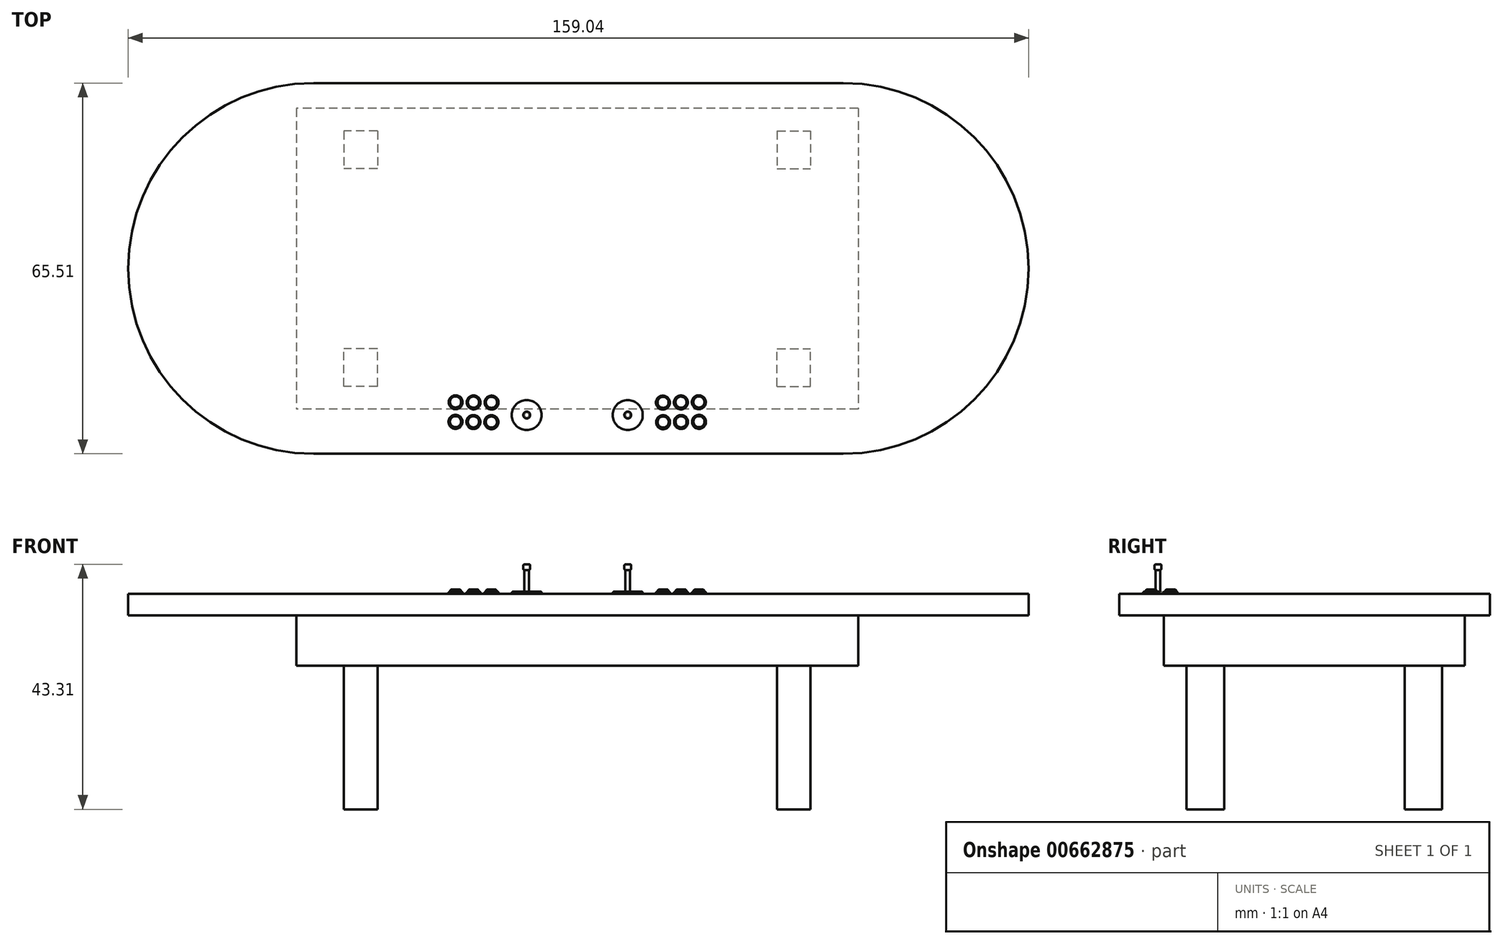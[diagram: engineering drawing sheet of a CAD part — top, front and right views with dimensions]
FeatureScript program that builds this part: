
annotation { "Feature Type Name" : "Feature", "Feature Type Description" : "" }
export const myFeature = defineFeature(function(context is Context, id is Id, definition is map)
    precondition{}
    {
        {
            var Q0;
            Q0=qCreatedBy(makeId("Top.planeOp"),FACE);
            var sketch = newSketch(context, id + "F0", { "sketchPlane" : qUnion([Q0])});
            skLineSegment(sketch, "E0.bottom", {"start": v(-46.56, 31.03) * mm, "end": v(46.96, 31.03) * mm});
            skLineSegment(sketch, "E0.top", {"start": v(-46.56, -34.48) * mm, "end": v(46.96, -34.48) * mm});
            skLineSegment(sketch, "E0.left", {"start": v(-46.56, 31.03) * mm, "end": v(-46.56, -34.48) * mm});
            skLineSegment(sketch, "E0.right", {"start": v(46.96, 31.03) * mm, "end": v(46.96, -34.48) * mm});
            skArc(sketch, "E1", {"start": v(46.96, 31.03) * mm, "mid": v(79.72, -1.72) * mm, "end": v(46.96, -34.48) * mm});
            skArc(sketch, "E2", {"start": v(-46.56, -34.48) * mm, "mid": v(-79.32, -1.72) * mm, "end": v(-46.56, 31.03) * mm});
            skSolve(sketch);
        }
        {
            var Q0;
            Q0=makeQuery(id+"F0.imprint","IMPRINT",FACE,{"disambiguationData":[TD([[makeQuery(id+"F0.imprint","IMPRINT",EDGE,{"derivedFrom":sQuery(id+"F0.wireOp",EDGE,"E0.bottom")}),-1.0]])]});
            var Q1;
            Q1=makeQuery(id+"F0.imprint","IMPRINT",FACE,{"disambiguationData":[TD([[makeQuery(id+"F0.imprint","IMPRINT",EDGE,{"derivedFrom":sQuery(id+"F0.wireOp",EDGE,"E0.left")}),-1.0]])]});
            var Q2;
            Q2=makeQuery(id+"F0.imprint","IMPRINT",FACE,{"disambiguationData":[TD([[makeQuery(id+"F0.imprint","IMPRINT",EDGE,{"derivedFrom":sQuery(id+"F0.wireOp",EDGE,"E0.right")}),1.0]])]});
            extrude(context, id + "F1", {"entities" : qUnion([Q0, Q1, Q2]), "depth" : 3.8 * mm, "offsetDistance" : 25.4 * mm});
        }
        {
            var Q0;
            Q0=makeQuery(id+"F1.opExtrude","CAP_FACE",FACE,{"disambiguationData":[OSD([sQuery(id+"F0.wireOp",EDGE,"E0.bottom"),sQuery(id+"F0.wireOp",EDGE,"E0.top"),sQuery(id+"F0.wireOp",EDGE,"E1"),sQuery(id+"F0.wireOp",EDGE,"E2")])],"isStart":true});
            var sketch = newSketch(context, id + "F2", { "sketchPlane" : qUnion([Q0])});
            skLineSegment(sketch, "E3.bottom", {"start": v(49.64, -26.58) * mm, "end": v(-49.64, -26.58) * mm});
            skLineSegment(sketch, "E3.top", {"start": v(49.64, 26.58) * mm, "end": v(-49.64, 26.58) * mm});
            skLineSegment(sketch, "E3.left", {"start": v(49.64, -26.58) * mm, "end": v(49.64, 26.58) * mm});
            skLineSegment(sketch, "E3.right", {"start": v(-49.64, -26.58) * mm, "end": v(-49.64, 26.58) * mm});
            skPoint(sketch, "E3.middle", {"position": v(0, 0) * mm});
            skSolve(sketch);
        }
        {
            var Q0;
            Q0 = qSketchRegion(id + "F2", true);
            extrude(context, id + "F3", {"entities" : qUnion([Q0]), "operationType" : NewBodyOperationType.ADD, "depth" : 8.9 * mm, "offsetDistance" : 25.4 * mm});
        }
        {
            var Q0;
            Q0=makeQuery(id+"F3.opExtrude","CAP_FACE",FACE,{"disambiguationData":[OSD([sQuery(id+"F2.wireOp",EDGE,"E3.bottom"),sQuery(id+"F2.wireOp",EDGE,"E3.top"),sQuery(id+"F2.wireOp",EDGE,"E3.left"),sQuery(id+"F2.wireOp",EDGE,"E3.right")])],"isStart":false});
            var sketch = newSketch(context, id + "F4", { "sketchPlane" : qUnion([Q0])});
            skLineSegment(sketch, "E4.bottom", {"start": v(-35.3, 22.55) * mm, "end": v(-41.22, 22.55) * mm});
            skLineSegment(sketch, "E4.top", {"start": v(-35.3, 15.93) * mm, "end": v(-41.22, 15.93) * mm});
            skLineSegment(sketch, "E4.left", {"start": v(-35.3, 22.55) * mm, "end": v(-35.3, 15.93) * mm});
            skLineSegment(sketch, "E4.right", {"start": v(-41.22, 22.55) * mm, "end": v(-41.22, 15.93) * mm});
            skPoint(sketch, "E4.middle", {"position": v(-38.26, 19.24) * mm});
            skLineSegment(sketch, "E5", {"start": v(0, 26.58) * mm, "end": v(0, -26.58) * mm, "construction": true});
            skLineSegment(sketch, "E6.MirrorCS", {"start": v(35.3, 22.55) * mm, "end": v(35.3, 15.93) * mm});
            skLineSegment(sketch, "E7.MirrorCS", {"start": v(35.3, 22.55) * mm, "end": v(41.22, 22.55) * mm});
            skLineSegment(sketch, "E8.MirrorCS", {"start": v(41.22, 22.55) * mm, "end": v(41.22, 15.93) * mm});
            skLineSegment(sketch, "E9.MirrorCS", {"start": v(35.3, 15.93) * mm, "end": v(41.22, 15.93) * mm});
            skLineSegment(sketch, "E10", {"start": v(-49.64, 0) * mm, "end": v(49.64, 0) * mm, "construction": true});
            skLineSegment(sketch, "E11.MirrorCS", {"start": v(-35.3, -15.93) * mm, "end": v(-41.22, -15.93) * mm});
            skLineSegment(sketch, "E12.MirrorCS", {"start": v(-41.22, -22.55) * mm, "end": v(-41.22, -15.93) * mm});
            skLineSegment(sketch, "E13.MirrorCS", {"start": v(-35.3, -22.55) * mm, "end": v(-41.22, -22.55) * mm});
            skLineSegment(sketch, "E14.MirrorCS", {"start": v(-35.3, -22.55) * mm, "end": v(-35.3, -15.93) * mm});
            skLineSegment(sketch, "E15.MirrorCS", {"start": v(35.3, -15.93) * mm, "end": v(41.22, -15.93) * mm});
            skLineSegment(sketch, "E16.MirrorCS", {"start": v(35.3, -22.55) * mm, "end": v(35.3, -15.93) * mm});
            skLineSegment(sketch, "E17.MirrorCS", {"start": v(35.3, -22.55) * mm, "end": v(41.22, -22.55) * mm});
            skLineSegment(sketch, "E18.MirrorCS", {"start": v(41.22, -22.55) * mm, "end": v(41.22, -15.93) * mm});
            skSolve(sketch);
        }
        {
            var Q0;
            Q0=makeQuery(id+"F4.imprint","IMPRINT",FACE,{"disambiguationData":[TD([[makeQuery(id+"F4.imprint","IMPRINT",EDGE,{"derivedFrom":sQuery(id+"F4.wireOp",EDGE,"E4.bottom")}),1.0]])]});
            var Q1;
            Q1=makeQuery(id+"F4.imprint","IMPRINT",FACE,{"disambiguationData":[TD([[makeQuery(id+"F4.imprint","IMPRINT",EDGE,{"derivedFrom":sQuery(id+"F4.wireOp",EDGE,"E6.MirrorCS")}),1.0]])]});
            var Q2;
            Q2=makeQuery(id+"F4.imprint","IMPRINT",FACE,{"disambiguationData":[TD([[makeQuery(id+"F4.imprint","IMPRINT",EDGE,{"derivedFrom":sQuery(id+"F4.wireOp",EDGE,"E15.MirrorCS")}),-1.0]])]});
            var Q3;
            Q3=makeQuery(id+"F4.imprint","IMPRINT",FACE,{"disambiguationData":[TD([[makeQuery(id+"F4.imprint","IMPRINT",EDGE,{"derivedFrom":sQuery(id+"F4.wireOp",EDGE,"E11.MirrorCS")}),1.0]])]});
            var Q4;
            Q4=sQuery(id+"F4.wireOp",EDGE,"E4.left");
            var Q5;
            Q5=sQuery(id+"F4.wireOp",EDGE,"E4.top");
            var Q6;
            Q6=sQuery(id+"F4.wireOp",EDGE,"E4.right");
            var Q7;
            Q7=sQuery(id+"F4.wireOp",EDGE,"E4.bottom");
            extrude(context, id + "F5", {"entities" : qUnion([Q0, Q1, Q2, Q3]), "operationType" : NewBodyOperationType.ADD, "surfaceEntities" : qUnion([Q4, Q5, Q6, Q7]), "depth" : 25.4 * mm, "offsetDistance" : 25.4 * mm});
        }
        {
            var Q0;
            Q0=makeQuery(id+"F1.opExtrude","CAP_FACE",FACE,{"disambiguationData":[OSD([sQuery(id+"F0.wireOp",EDGE,"E0.bottom"),sQuery(id+"F0.wireOp",EDGE,"E0.top"),sQuery(id+"F0.wireOp",EDGE,"E1"),sQuery(id+"F0.wireOp",EDGE,"E2")])],"isStart":false});
            var sketch = newSketch(context, id + "F6", { "sketchPlane" : qUnion([Q0])});
            skCircle(sketch, "E19", {"center": v(-15.16, -28.9) * mm, "radius": 1.23 * mm});
            skCircle(sketch, "E20.0.1.0", {"center": v(-15.13, -25.42) * mm, "radius": 1.23 * mm});
            skCircle(sketch, "E20.1.0.0", {"center": v(-18.34, -28.86) * mm, "radius": 1.23 * mm});
            skCircle(sketch, "E20.1.1.0", {"center": v(-18.3, -25.4) * mm, "radius": 1.23 * mm});
            skCircle(sketch, "E20.2.0.0", {"center": v(-21.5, -28.83) * mm, "radius": 1.23 * mm});
            skCircle(sketch, "E20.2.1.0", {"center": v(-21.48, -25.36) * mm, "radius": 1.23 * mm});
            skLineSegment(sketch, "E20.direction1", {"start": v(-15.16, -28.9) * mm, "end": v(-18.34, -28.86) * mm, "construction": true});
            skLineSegment(sketch, "E20.direction2", {"start": v(-15.16, -28.9) * mm, "end": v(-15.13, -25.42) * mm, "construction": true});
            skLineSegment(sketch, "E21", {"start": v(0, -30.78) * mm, "end": v(0, -16.96) * mm, "construction": true});
            skCircle(sketch, "E22.MirrorC", {"center": v(21.5, -28.83) * mm, "radius": 1.23 * mm});
            skCircle(sketch, "E23.MirrorC", {"center": v(18.34, -28.86) * mm, "radius": 1.23 * mm});
            skCircle(sketch, "E24.MirrorC", {"center": v(21.48, -25.36) * mm, "radius": 1.23 * mm});
            skCircle(sketch, "E25.MirrorC", {"center": v(18.3, -25.4) * mm, "radius": 1.23 * mm});
            skCircle(sketch, "E26.MirrorC", {"center": v(15.13, -25.42) * mm, "radius": 1.23 * mm});
            skCircle(sketch, "E27.MirrorC", {"center": v(15.16, -28.9) * mm, "radius": 1.23 * mm});
            skCircle(sketch, "E28", {"center": v(8.92, -27.62) * mm, "radius": 2.64 * mm});
            skCircle(sketch, "E29.MirrorC", {"center": v(-8.92, -27.62) * mm, "radius": 2.64 * mm});
            skSolve(sketch);
        }
        {
            var Q0;
            Q0 = qSketchRegion(id + "F6", true);
            extrude(context, id + "F7", {"entities" : qUnion([Q0]), "operationType" : NewBodyOperationType.ADD, "depth" : 0.38 * mm, "offsetDistance" : 25.4 * mm});
        }
        {
            var Q0;
            Q0=makeQuery(id+"F7.opExtrude","CAP_FACE",FACE,{"disambiguationData":[OSD([sQuery(id+"F6.wireOp",EDGE,"E28")])],"isStart":false});
            var sketch = newSketch(context, id + "F8", { "sketchPlane" : qUnion([Q0])});
            skCircle(sketch, "E30", {"center": v(21.5, -28.8) * mm, "radius": 0.98 * mm});
            skCircle(sketch, "E31.0.1.0", {"center": v(21.5, -25.32) * mm, "radius": 0.98 * mm});
            skCircle(sketch, "E31.1.0.0", {"center": v(18.34, -28.83) * mm, "radius": 0.98 * mm});
            skCircle(sketch, "E31.1.1.0", {"center": v(18.33, -25.35) * mm, "radius": 0.98 * mm});
            skCircle(sketch, "E31.2.0.0", {"center": v(15.17, -28.86) * mm, "radius": 0.98 * mm});
            skCircle(sketch, "E31.2.1.0", {"center": v(15.16, -25.38) * mm, "radius": 0.98 * mm});
            skLineSegment(sketch, "E31.direction1", {"start": v(21.5, -28.8) * mm, "end": v(18.34, -28.83) * mm, "construction": true});
            skLineSegment(sketch, "E31.direction2", {"start": v(21.5, -28.8) * mm, "end": v(21.5, -25.32) * mm, "construction": true});
            skLineSegment(sketch, "E32", {"start": v(0, -34.63) * mm, "end": v(0, -24.38) * mm, "construction": true});
            skCircle(sketch, "E33.MirrorC", {"center": v(-15.17, -28.86) * mm, "radius": 0.98 * mm});
            skCircle(sketch, "E34.MirrorC", {"center": v(-15.16, -25.38) * mm, "radius": 0.98 * mm});
            skCircle(sketch, "E35.MirrorC", {"center": v(-18.33, -25.35) * mm, "radius": 0.98 * mm});
            skCircle(sketch, "E36.MirrorC", {"center": v(-18.34, -28.83) * mm, "radius": 0.98 * mm});
            skCircle(sketch, "E37.MirrorC", {"center": v(-21.5, -28.8) * mm, "radius": 0.98 * mm});
            skCircle(sketch, "E38.MirrorC", {"center": v(-21.5, -25.32) * mm, "radius": 0.98 * mm});
            skSolve(sketch);
        }
        {
            var Q0;
            Q0 = qSketchRegion(id + "F8", true);
            extrude(context, id + "F9", {"entities" : qUnion([Q0]), "operationType" : NewBodyOperationType.ADD, "depth" : 0.38 * mm, "offsetDistance" : 25.4 * mm});
        }
        {
            var Q0;
            Q0=makeQuery(id+"F7.opExtrude","CAP_EDGE",EDGE,{"disambiguationData":[OSD([sQuery(id+"F6.wireOp",EDGE,"E20.2.0.0")])],"isStart":false});
            var Q1;
            Q1=makeQuery(id+"F7.opExtrude","CAP_EDGE",EDGE,{"disambiguationData":[OSD([sQuery(id+"F6.wireOp",EDGE,"E20.1.0.0")])],"isStart":false});
            var Q2;
            Q2=makeQuery(id+"F7.opExtrude","CAP_EDGE",EDGE,{"disambiguationData":[OSD([sQuery(id+"F6.wireOp",EDGE,"E19")])],"isStart":false});
            var Q3;
            Q3=makeQuery(id+"F7.opExtrude","CAP_EDGE",EDGE,{"disambiguationData":[OSD([sQuery(id+"F6.wireOp",EDGE,"E20.0.1.0")])],"isStart":false});
            var Q4;
            Q4=makeQuery(id+"F7.opExtrude","CAP_EDGE",EDGE,{"disambiguationData":[OSD([sQuery(id+"F6.wireOp",EDGE,"E20.2.1.0")])],"isStart":false});
            var Q5;
            Q5=makeQuery(id+"F7.opExtrude","CAP_EDGE",EDGE,{"disambiguationData":[OSD([sQuery(id+"F6.wireOp",EDGE,"E20.1.1.0")])],"isStart":false});
            var Q6;
            Q6=makeQuery(id+"F7.opExtrude","CAP_EDGE",EDGE,{"disambiguationData":[OSD([sQuery(id+"F6.wireOp",EDGE,"E22.MirrorC")])],"isStart":false});
            var Q7;
            Q7=makeQuery(id+"F7.opExtrude","CAP_EDGE",EDGE,{"disambiguationData":[OSD([sQuery(id+"F6.wireOp",EDGE,"E24.MirrorC")])],"isStart":false});
            var Q8;
            Q8=makeQuery(id+"F7.opExtrude","CAP_EDGE",EDGE,{"disambiguationData":[OSD([sQuery(id+"F6.wireOp",EDGE,"E27.MirrorC")])],"isStart":false});
            var Q9;
            Q9=makeQuery(id+"F7.opExtrude","CAP_EDGE",EDGE,{"disambiguationData":[OSD([sQuery(id+"F6.wireOp",EDGE,"E25.MirrorC")])],"isStart":false});
            var Q10;
            Q10=makeQuery(id+"F7.opExtrude","CAP_EDGE",EDGE,{"disambiguationData":[OSD([sQuery(id+"F6.wireOp",EDGE,"E26.MirrorC")])],"isStart":false});
            var Q11;
            Q11=makeQuery(id+"F7.opExtrude","CAP_EDGE",EDGE,{"disambiguationData":[OSD([sQuery(id+"F6.wireOp",EDGE,"E29.MirrorC")])],"isStart":false});
            var Q12;
            Q12=makeQuery(id+"F7.opExtrude","CAP_EDGE",EDGE,{"disambiguationData":[OSD([sQuery(id+"F6.wireOp",EDGE,"E28")])],"isStart":false});
            var Q13;
            Q13=makeQuery(id+"F7.opExtrude","CAP_EDGE",EDGE,{"disambiguationData":[OSD([sQuery(id+"F6.wireOp",EDGE,"E23.MirrorC")])],"isStart":false});
            fillet(context, id + "F10", {"entities" : qUnion([Q0, Q1, Q2, Q3, Q4, Q5, Q6, Q7, Q8, Q9, Q10, Q11, Q12, Q13]), "radius" : 0.25 * mm, "tangentPropagation" : true, "allowEdgeOverflow" : false});
        }
        {
            var Q0;
            Q0=makeQuery(id+"F9.opExtrude","CAP_EDGE",EDGE,{"disambiguationData":[OSD([sQuery(id+"F8.wireOp",EDGE,"E37.MirrorC")])],"isStart":false});
            var Q1;
            Q1=makeQuery(id+"F9.opExtrude","CAP_EDGE",EDGE,{"disambiguationData":[OSD([sQuery(id+"F8.wireOp",EDGE,"E38.MirrorC")])],"isStart":false});
            var Q2;
            Q2=makeQuery(id+"F9.opExtrude","CAP_EDGE",EDGE,{"disambiguationData":[OSD([sQuery(id+"F8.wireOp",EDGE,"E35.MirrorC")])],"isStart":false});
            var Q3;
            Q3=makeQuery(id+"F9.opExtrude","CAP_EDGE",EDGE,{"disambiguationData":[OSD([sQuery(id+"F8.wireOp",EDGE,"E36.MirrorC")])],"isStart":false});
            var Q4;
            Q4=makeQuery(id+"F9.opExtrude","CAP_EDGE",EDGE,{"disambiguationData":[OSD([sQuery(id+"F8.wireOp",EDGE,"E34.MirrorC")])],"isStart":false});
            var Q5;
            Q5=makeQuery(id+"F9.opExtrude","CAP_EDGE",EDGE,{"disambiguationData":[OSD([sQuery(id+"F8.wireOp",EDGE,"E33.MirrorC")])],"isStart":false});
            var Q6;
            Q6=makeQuery(id+"F9.opExtrude","CAP_EDGE",EDGE,{"disambiguationData":[OSD([sQuery(id+"F8.wireOp",EDGE,"E31.2.1.0")])],"isStart":false});
            var Q7;
            Q7=makeQuery(id+"F9.opExtrude","CAP_EDGE",EDGE,{"disambiguationData":[OSD([sQuery(id+"F8.wireOp",EDGE,"E31.2.0.0")])],"isStart":false});
            var Q8;
            Q8=makeQuery(id+"F9.opExtrude","CAP_EDGE",EDGE,{"disambiguationData":[OSD([sQuery(id+"F8.wireOp",EDGE,"E31.1.1.0")])],"isStart":false});
            var Q9;
            Q9=makeQuery(id+"F9.opExtrude","CAP_EDGE",EDGE,{"disambiguationData":[OSD([sQuery(id+"F8.wireOp",EDGE,"E31.1.0.0")])],"isStart":false});
            var Q10;
            Q10=makeQuery(id+"F9.opExtrude","CAP_EDGE",EDGE,{"disambiguationData":[OSD([sQuery(id+"F8.wireOp",EDGE,"E30")])],"isStart":false});
            var Q11;
            Q11=makeQuery(id+"F9.opExtrude","CAP_EDGE",EDGE,{"disambiguationData":[OSD([sQuery(id+"F8.wireOp",EDGE,"E31.0.1.0")])],"isStart":false});
            fillet(context, id + "F11", {"entities" : qUnion([Q0, Q1, Q2, Q3, Q4, Q5, Q6, Q7, Q8, Q9, Q10, Q11]), "radius" : 0.38 * mm, "tangentPropagation" : true, "allowEdgeOverflow" : false});
        }
        {
            var Q0;
            Q0=makeQuery(id+"F7.opExtrude","CAP_FACE",FACE,{"disambiguationData":[OSD([sQuery(id+"F6.wireOp",EDGE,"E29.MirrorC")])],"isStart":false});
            var sketch = newSketch(context, id + "F12", { "sketchPlane" : qUnion([Q0])});
            skCircle(sketch, "E39", {"center": v(-8.92, -27.62) * mm, "radius": 0.41 * mm});
            skLineSegment(sketch, "E40", {"start": v(0, -34.14) * mm, "end": v(0, -25.28) * mm, "construction": true});
            skCircle(sketch, "E41.MirrorC", {"center": v(8.92, -27.62) * mm, "radius": 0.41 * mm});
            skSolve(sketch);
        }
        {
            var Q0;
            Q0 = qSketchRegion(id + "F12", true);
            extrude(context, id + "F13", {"entities" : qUnion([Q0]), "operationType" : NewBodyOperationType.ADD, "depth" : 3.8 * mm, "offsetDistance" : 25.4 * mm});
        }
        {
            var Q0;
            Q0=makeQuery(id+"F13.opExtrude","CAP_FACE",FACE,{"disambiguationData":[OSD([sQuery(id+"F12.wireOp",EDGE,"E39")])],"isStart":false});
            var sketch = newSketch(context, id + "F14", { "sketchPlane" : qUnion([Q0])});
            skCircle(sketch, "E42", {"center": v(-8.92, -27.62) * mm, "radius": 0.62 * mm});
            skLineSegment(sketch, "E43", {"start": v(0, -34.4) * mm, "end": v(0, -21.6) * mm, "construction": true});
            skCircle(sketch, "E44.MirrorC", {"center": v(8.92, -27.62) * mm, "radius": 0.62 * mm});
            skSolve(sketch);
        }
        {
            var Q0;
            Q0 = qSketchRegion(id + "F14", true);
            extrude(context, id + "F15", {"entities" : qUnion([Q0]), "operationType" : NewBodyOperationType.ADD, "depth" : 1.02 * mm, "offsetDistance" : 25.4 * mm});
        }
        {
            var Q0;
            Q0=makeQuery(id+"F15.opExtrude","CAP_EDGE",EDGE,{"disambiguationData":[OSD([sQuery(id+"F14.wireOp",EDGE,"E42")])],"isStart":true});
            var Q1;
            Q1=makeQuery(id+"F15.opExtrude","CAP_EDGE",EDGE,{"disambiguationData":[OSD([sQuery(id+"F14.wireOp",EDGE,"E42")])],"isStart":false});
            var Q2;
            Q2=makeQuery(id+"F15.opExtrude","CAP_EDGE",EDGE,{"disambiguationData":[OSD([sQuery(id+"F14.wireOp",EDGE,"E44.MirrorC")])],"isStart":false});
            var Q3;
            Q3=makeQuery(id+"F15.opExtrude","CAP_EDGE",EDGE,{"disambiguationData":[OSD([sQuery(id+"F14.wireOp",EDGE,"E44.MirrorC")])],"isStart":true});
            fillet(context, id + "F16", {"entities" : qUnion([Q0, Q1, Q2, Q3]), "radius" : 0.25 * mm, "tangentPropagation" : true, "allowEdgeOverflow" : false});
        }
    });
